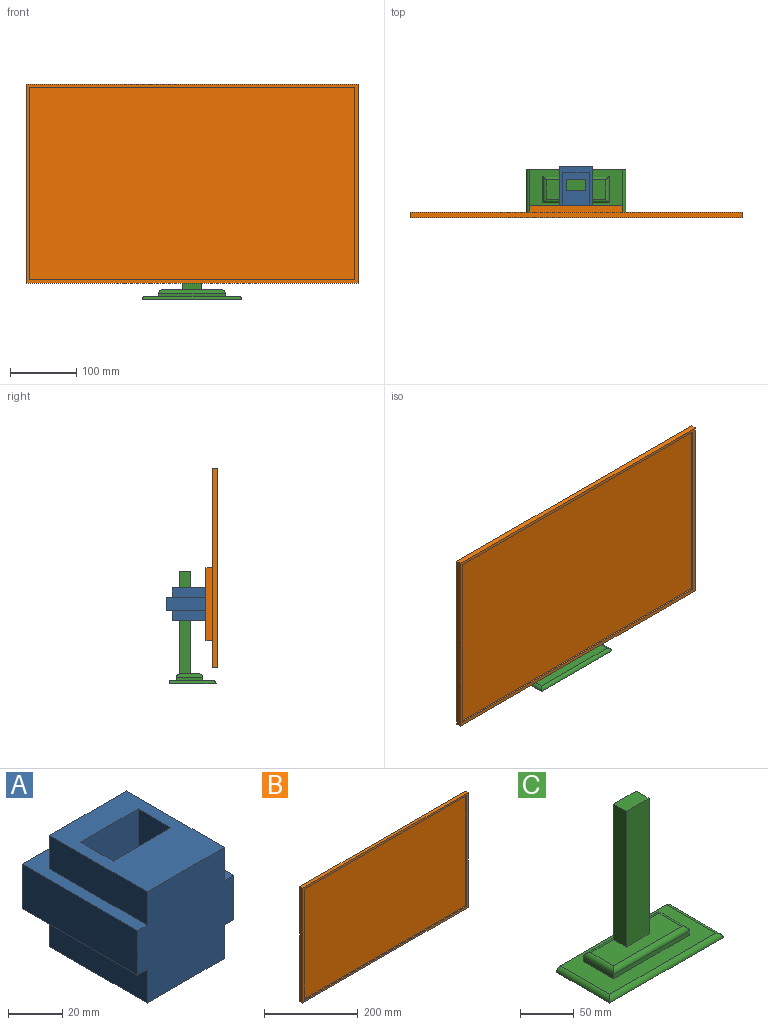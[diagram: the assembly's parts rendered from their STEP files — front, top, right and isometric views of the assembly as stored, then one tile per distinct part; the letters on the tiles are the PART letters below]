
ASSEMBLY  parts=3 mates=2
PART A: 18 faces, bbox 50x60x50 mm
  f0: plane 60x20mm, normal (1,0,0), area 1200mm2, adj f1,f3,f4,f13
  f1: plane 50x20mm, normal (0,1,0), area 1000mm2, adj f0,f2,f4,f13
  f2: plane 60x20mm, normal (-1,0,0), area 1200mm2, adj f1,f3,f4,f13
  f3: plane 50x50mm, normal (0,-1,0), area 2200mm2, adj f0,f2,f4,f5,f11,f12,f13,f14
  f4: plane 60x50mm, normal (0,0,1), area 969.2mm2, adj f0,f1,f2,f3,f5,f6,f11
  f5: plane 50.77x15mm, normal (1,0,0), area 761.5mm2, adj f3,f4,f6,f12
  f6: plane 40x15mm, normal (0,1,0), area 600mm2, adj f4,f5,f11,f12
  f7: plane 50x17mm, normal (-1,0,0), area 850mm2, adj f8,f10,f12,f17
  f8: plane 50x30mm, normal (0,1,0), area 1500mm2, adj f7,f9,f12,f17
  f9: plane 50x17mm, normal (1,0,0), area 850mm2, adj f8,f10,f12,f17
  f10: plane 50x30mm, normal (0,-1,0), area 1500mm2, adj f7,f9,f12,f17
  f11: plane 50.77x15mm, normal (-1,0,0), area 761.5mm2, adj f3,f4,f6,f12
  f12: plane 50.77x40mm, normal (0,0,1), area 1520.8mm2, adj f3,f5,f6,f7,f8,f9,f10,f11
  f13: plane 60x50mm, normal (0,0,-1), area 969.2mm2, adj f0,f1,f2,f3,f14,f15,f16
  f14: plane 50.77x15mm, normal (1,0,0), area 761.5mm2, adj f3,f13,f15,f17
  f15: plane 40x15mm, normal (0,1,0), area 600mm2, adj f13,f14,f16,f17
  f16: plane 50.77x15mm, normal (-1,0,0), area 761.5mm2, adj f3,f13,f15,f17
  f17: plane 50.77x40mm, normal (0,0,-1), area 1520.8mm2, adj f3,f7,f8,f9,f10,f14,f15,f16
PART B: 16 faces, bbox 500x18x300 mm
  f0: plane 500x300mm, normal (0,-1,0), area 7900mm2, adj f1,f2,f3,f4,f6,f7,f8,f9
  f1: plane 500x8mm, normal (0,0,-1), area 4000mm2, adj f0,f2,f4,f5
  f2: plane 300x8mm, normal (1,0,0), area 2400mm2, adj f0,f1,f3,f5
  f3: plane 500x8mm, normal (0,0,1), area 4000mm2, adj f0,f2,f4,f5
  f4: plane 300x8mm, normal (-1,0,0), area 2400mm2, adj f0,f1,f3,f5
  f5: plane 500x300mm, normal (0,1,0), area 134600mm2, adj f1,f2,f3,f4,f11,f12,f13,f14
  f6: plane 490x3mm, normal (0,0,1), area 1470mm2, adj f0,f7,f9,f10
  f7: plane 290x3mm, normal (-1,0,0), area 870mm2, adj f0,f6,f8,f10
  f8: plane 490x3mm, normal (0,0,-1), area 1470mm2, adj f0,f7,f9,f10
  f9: plane 290x3mm, normal (1,0,0), area 870mm2, adj f0,f6,f8,f10
  f10: plane 490x290mm, normal (0,-1,0), area 142100mm2, adj f6,f7,f8,f9
  f11: plane 140x10mm, normal (0,0,-1), area 1400mm2, adj f5,f12,f14,f15
  f12: plane 110x10mm, normal (-1,0,0), area 1100mm2, adj f5,f11,f13,f15
  f13: plane 140x10mm, normal (0,0,1), area 1400mm2, adj f5,f12,f14,f15
  f14: plane 110x10mm, normal (1,0,0), area 1100mm2, adj f5,f11,f13,f15
  f15: plane 140x110mm, normal (0,1,0), area 15400mm2, adj f11,f12,f13,f14
PART C: 20 faces, bbox 150x70x170 mm
  f0: plane 150x5mm, normal (0,1,0), area 739.3mm2, adj f1,f2,f17,f19
  f1: plane 140x65mm, normal (0,0,1), area 5100mm2, adj f0,f3,f4,f5,f6,f17,f18,f19
  f2: plane 150x70mm, normal (0,0,-1), area 10500mm2, adj f0,f17,f18,f19
  f3: plane 100x5mm, normal (0,-1,0), area 500mm2, adj f1,f4,f6,f15
  f4: plane 40x5mm, normal (1,0,0), area 200mm2, adj f1,f3,f5,f16
  f5: plane 100x5mm, normal (0,1,0), area 500mm2, adj f1,f4,f6,f14
  f6: plane 40x5mm, normal (-1,0,0), area 200mm2, adj f1,f3,f5,f13
  f7: plane 90x30mm, normal (0,0,1), area 2190mm2, adj f9,f11,f12,f13,f14,f15,f16
  f8: plane 30x17mm, normal (0,0,1), area 510mm2, adj f9,f10,f11,f12
  f9: plane 155x17mm, normal (-1,0,0), area 2635mm2, adj f7,f8,f10,f12
  f10: plane 155x30mm, normal (0,1,0), area 4650mm2, adj f8,f9,f11,f14
  f11: plane 155x17mm, normal (1,0,0), area 2635mm2, adj f7,f8,f10,f12
  f12: plane 155x30mm, normal (0,-1,0), area 4650mm2, adj f7,f8,f9,f11
  f13: cylinder r=5mm len=40mm, axis (0,-1,0), area 285.6mm2, adj f6,f7,f14,f15
  f14: cylinder r=5mm len=100mm, axis (-1,0,0), area 756.9mm2, adj f5,f7,f10,f13,f16
  f15: cylinder r=5mm len=100mm, axis (1,0,0), area 756.9mm2, adj f3,f7,f13,f16
  f16: cylinder r=5mm len=40mm, axis (0,1,0), area 285.6mm2, adj f4,f7,f14,f15
  f17: cylinder r=5mm len=70mm, axis (0,-1,0), area 535.5mm2, adj f0,f1,f2,f18
  f18: cylinder r=5mm len=150mm, axis (1,0,0), area 1149.6mm2, adj f1,f2,f17,f19
  f19: cylinder r=5mm len=70mm, axis (0,1,0), area 535.5mm2, adj f0,f1,f2,f18
PLACE A t=(-7.34,27.96,120.06)mm
PLACE B t=(-5.73,-29.7,181.69)mm
PLACE C t=(-15,-33.8,0)mm
MATE slider A.f12 <-> C.f8  axis (0,0,1) through (0,11.5,145.06)mm
MATE fastened B.f15 <-> A.f3  axis (0,1,0) through (0,-19.7,120.06)mm
